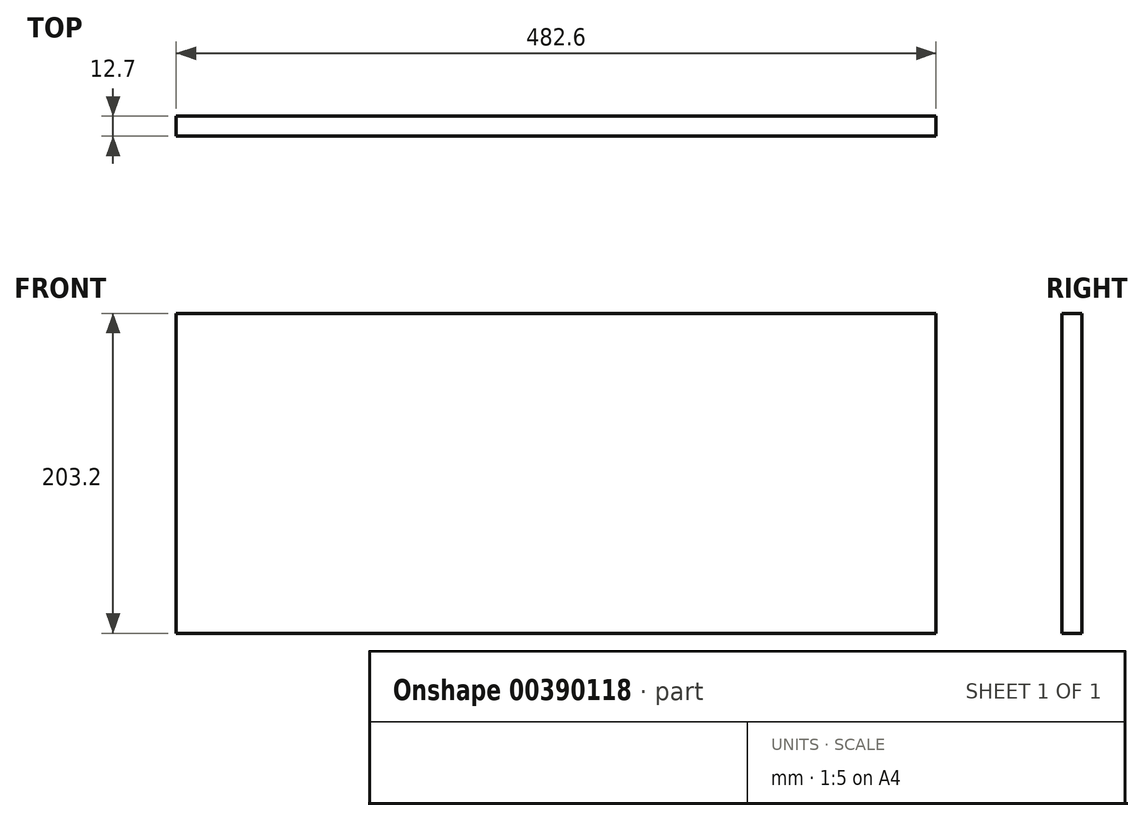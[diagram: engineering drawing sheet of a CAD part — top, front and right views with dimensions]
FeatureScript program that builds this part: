
annotation { "Feature Type Name" : "Feature", "Feature Type Description" : "" }
export const myFeature = defineFeature(function(context is Context, id is Id, definition is map)
    precondition{}
    {
        {
            var Q0;
            Q0=qCreatedBy(makeId("Front.planeOp"),FACE);
            var sketch = newSketch(context, id + "F0", { "sketchPlane" : qUnion([Q0])});
            skLineSegment(sketch, "E0.bottom", {"start": v(0, 203.2) * mm, "end": v(482.6, 203.2) * mm});
            skLineSegment(sketch, "E0.top", {"start": v(0, 0) * mm, "end": v(482.6, 0) * mm});
            skLineSegment(sketch, "E0.left", {"start": v(0, 203.2) * mm, "end": v(0, 0) * mm});
            skLineSegment(sketch, "E0.right", {"start": v(482.6, 203.2) * mm, "end": v(482.6, 0) * mm});
            skSolve(sketch);
        }
        {
            var Q0;
            Q0 = qSketchRegion(id + "F0", true);
            extrude(context, id + "F1", {"entities" : qUnion([Q0]), "depth" : 12.7 * mm});
        }
    });
